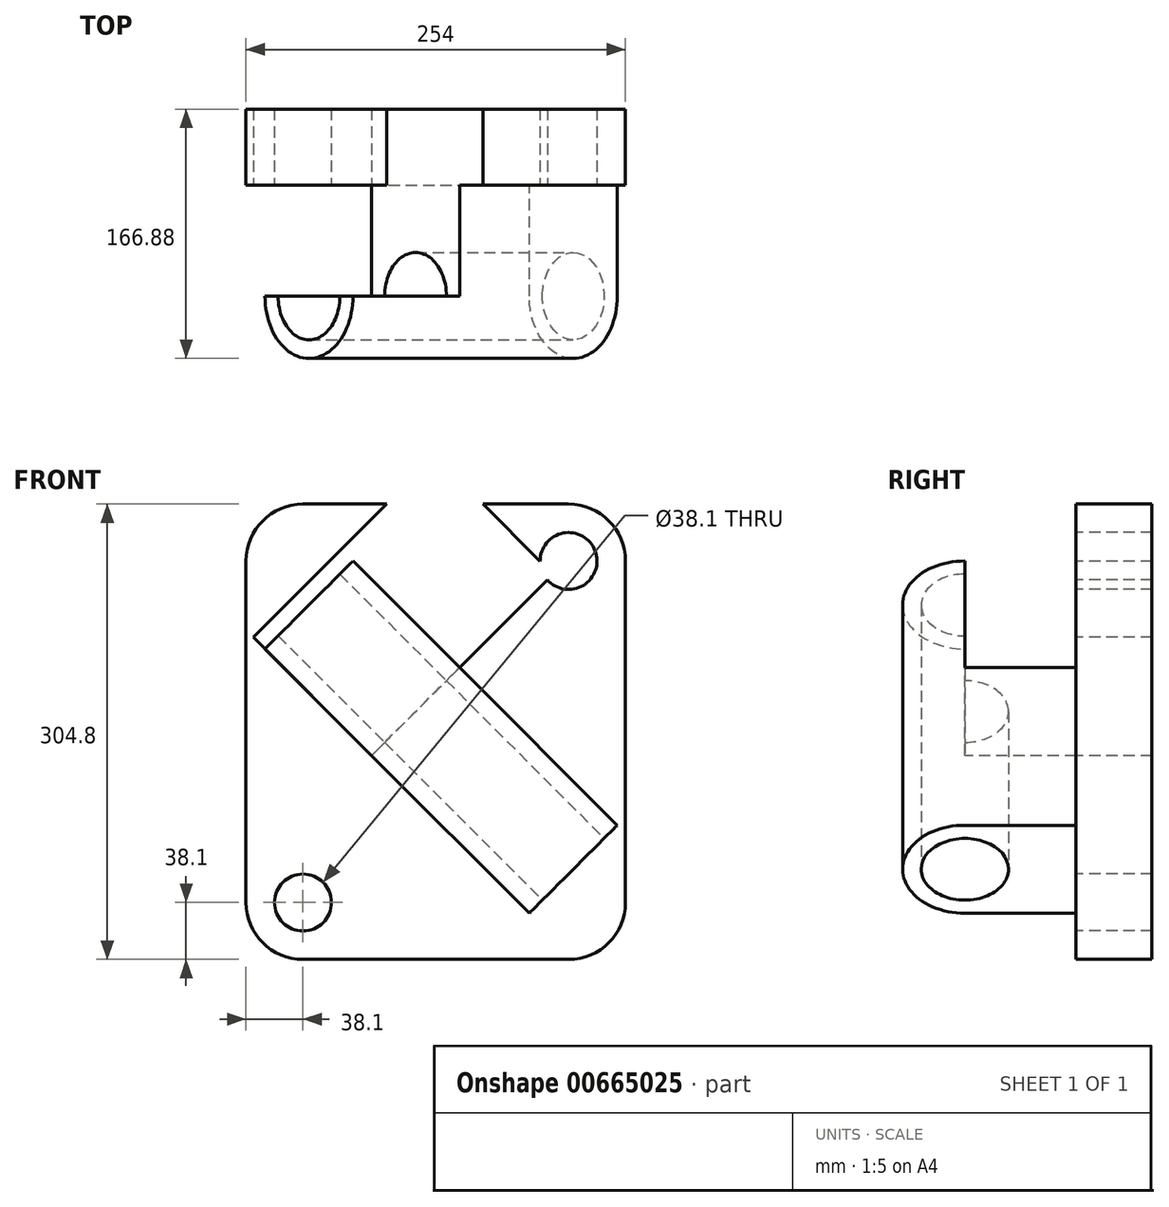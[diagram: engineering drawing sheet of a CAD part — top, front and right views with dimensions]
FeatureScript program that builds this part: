
annotation { "Feature Type Name" : "Feature", "Feature Type Description" : "" }
export const myFeature = defineFeature(function(context is Context, id is Id, definition is map)
    precondition{}
    {
        {
            var Q0;
            Q0=qCreatedBy(makeId("Front.planeOp"),FACE);
            var sketch = newSketch(context, id + "F0", { "sketchPlane" : qUnion([Q0])});
            skLineSegment(sketch, "E0", {"start": v(38.1, 0) * mm, "end": v(215.9, 0) * mm});
            skLineSegment(sketch, "E1", {"start": v(254, 38.1) * mm, "end": v(254, 266.7) * mm});
            skLineSegment(sketch, "E2", {"start": v(215.9, 304.8) * mm, "end": v(38.1, 304.8) * mm});
            skLineSegment(sketch, "E3", {"start": v(0, 266.7) * mm, "end": v(0, 38.1) * mm});
            skPoint(sketch, "E4.visualSharp", {"position": v(0, 304.8) * mm});
            skArc(sketch, "E4.filletArc", {"start": v(38.1, 304.8) * mm, "mid": v(11.16, 293.64) * mm, "end": v(0, 266.7) * mm});
            skPoint(sketch, "E5.visualSharp", {"position": v(254, 304.8) * mm});
            skArc(sketch, "E5.filletArc", {"start": v(254, 266.7) * mm, "mid": v(242.84, 293.64) * mm, "end": v(215.9, 304.8) * mm});
            skPoint(sketch, "E6.visualSharp", {"position": v(254, 0) * mm});
            skArc(sketch, "E6.filletArc", {"start": v(215.9, 0) * mm, "mid": v(242.84, 11.16) * mm, "end": v(254, 38.1) * mm});
            skPoint(sketch, "E7.visualSharp", {"position": v(0, 0) * mm});
            skArc(sketch, "E7.filletArc", {"start": v(0, 38.1) * mm, "mid": v(11.16, 11.16) * mm, "end": v(38.1, 0) * mm});
            skCircle(sketch, "E8", {"center": v(38.1, 38.1) * mm, "radius": 19.05 * mm});
            skCircle(sketch, "E9", {"center": v(215.9, 266.7) * mm, "radius": 19.05 * mm});
            skLineSegment(sketch, "E10", {"start": v(189.58, 30.9) * mm, "end": v(12.67, 207.81) * mm});
            skLineSegment(sketch, "E11.0", {"start": v(248.5, 89.81) * mm, "end": v(71.58, 266.73) * mm});
            skLineSegment(sketch, "E12", {"start": v(248.5, 89.81) * mm, "end": v(189.58, 30.9) * mm});
            skLineSegment(sketch, "E13", {"start": v(12.67, 207.81) * mm, "end": v(71.58, 266.73) * mm});
            skLineSegment(sketch, "E14", {"start": v(0, 38.1) * mm, "end": v(189.58, 30.9) * mm});
            skSolve(sketch);
        }
        {
            var Q0;
            Q0=makeQuery(id+"F0.imprint","IMPRINT",FACE,{"disambiguationData":[TD([[makeQuery(id+"F0.imprint","IMPRINT",EDGE,{"derivedFrom":sQuery(id+"F0.wireOp",EDGE,"E0")}),1.0]])]});
            var Q1;
            Q1=makeQuery(id+"F0.imprint","IMPRINT",FACE,{"disambiguationData":[TD([[makeQuery(id+"F0.imprint","IMPRINT",EDGE,{"derivedFrom":sQuery(id+"F0.wireOp",EDGE,"E10")}),-1.0]])]});
            extrude(context, id + "F1", {"entities" : qUnion([Q0, Q1]), "endBound" : BoundingType.SYMMETRIC, "oppositeDirection" : true, "depth" : 50.8 * mm, "offsetDistance" : 25.4 * mm});
        }
        {
            var Q0;
            Q0=makeQuery(id+"F0.imprint","IMPRINT",FACE,{"disambiguationData":[TD([[makeQuery(id+"F0.imprint","IMPRINT",EDGE,{"derivedFrom":sQuery(id+"F0.wireOp",EDGE,"E10")}),-1.0]])]});
            extrude(context, id + "F2", {"entities" : qUnion([Q0]), "operationType" : NewBodyOperationType.ADD, "depth" : 99.82 * mm, "offsetDistance" : 25.4 * mm});
        }
        {
            var Q0;
            Q0=makeQuery(id+"F2.opExtrude","SWEPT_FACE",FACE,{"disambiguationData":[OSD([sQuery(id+"F0.wireOp",EDGE,"E12")])]});
            var sketch = newSketch(context, id + "F3", { "sketchPlane" : qUnion([Q0])});
            skCircle(sketch, "E15", {"center": v(-99.82, 197.56) * mm, "radius": 29.21 * mm});
            skCircle(sketch, "E16", {"center": v(-99.82, 197.56) * mm, "radius": 41.66 * mm});
            skSolve(sketch);
        }
        {
            var Q0;
            {var subQ0=sQuery(id+"F3.wireOp",EDGE,"E15");var subQ1=sQuery(id+"F0.wireOp",EDGE,"E12");var subQ2=makeQuery(id+"F2.opExtrude","CAP_EDGE",EDGE,{"disambiguationData":[OSD([subQ1])],"isStart":false});var subQ3=makeQuery(id+"F3.imprint","INTERSECT",VERTEX,{"disambiguationData":[OD(0.0)],"derivedFrom":[subQ2,subQ0]});Q0=makeQuery(id+"F3.imprint","IMPRINT",FACE,{"disambiguationData":[TD([[makeQuery(id+"F3.imprint","IMPRINT",EDGE,{"disambiguationData":[TD([[subQ3,1.0]])],"derivedFrom":subQ0}),-1.0]])]});}
            extrude(context, id + "F4", {"entities" : qUnion([Q0]), "operationType" : NewBodyOperationType.ADD, "oppositeDirection" : true, "depth" : 250.2 * mm, "offsetDistance" : 25.4 * mm});
        }
        {
            var Q0;
            {var subQ0=sQuery(id+"F3.wireOp",EDGE,"48uWv1ek-4zHe-EfZB-hBq6-6IiOLvBYJ8zC");var subQ1=makeQuery(id+"F2.opExtrude","CAP_EDGE",EDGE,{"disambiguationData":[OSD([sQuery(id+"F0.wireOp",EDGE,"E12")])],"isStart":false});var subQ2=makeQuery(id+"F3.imprint","INTERSECT",VERTEX,{"disambiguationData":[OD(0.0)],"derivedFrom":[subQ1,subQ0]});Q0=makeQuery(id+"F3.imprint","IMPRINT",FACE,{"disambiguationData":[TD([[makeQuery(id+"F3.imprint","IMPRINT",EDGE,{"disambiguationData":[TD([[subQ2,-1.0]])],"derivedFrom":subQ0}),1.0]])]});}
            var Q1;
            {var subQ0=sQuery(id+"F3.wireOp",EDGE,"E15");var subQ1=makeQuery(id+"F2.opExtrude","CAP_EDGE",EDGE,{"disambiguationData":[OSD([sQuery(id+"F0.wireOp",EDGE,"E12")])],"isStart":false});var subQ2=makeQuery(id+"F3.imprint","INTERSECT",VERTEX,{"disambiguationData":[OD(0.0)],"derivedFrom":[subQ1,subQ0]});Q1=makeQuery(id+"F3.imprint","IMPRINT",FACE,{"disambiguationData":[TD([[makeQuery(id+"F3.imprint","IMPRINT",EDGE,{"disambiguationData":[TD([[subQ2,-1.0]])],"derivedFrom":subQ0}),1.0]])]});}
            extrude(context, id + "F5", {"entities" : qUnion([Q0, Q1]), "operationType" : NewBodyOperationType.REMOVE, "oppositeDirection" : true, "depth" : 250.2 * mm, "offsetDistance" : 25.4 * mm});
        }
        {
            var Q0;
            Q0=makeQuery(id+"F2.opExtrude","SWEPT_FACE",FACE,{"disambiguationData":[OSD([sQuery(id+"F0.wireOp",EDGE,"E10")])]});
            var sketch = newSketch(context, id + "F6", { "sketchPlane" : qUnion([Q0])});
            skLineSegment(sketch, "E17.0", {"start": v(-137.99, 37.08) * mm, "end": v(112.2, 37.08) * mm});
            skLineSegment(sketch, "E18", {"start": v(-137.99, 37.08) * mm, "end": v(-93.54, 37.08) * mm});
            skLineSegment(sketch, "E19", {"start": v(-93.54, 37.08) * mm, "end": v(-93.54, 149.02) * mm});
            skLineSegment(sketch, "E20", {"start": v(-93.54, 149.02) * mm, "end": v(67.75, 149.02) * mm});
            skLineSegment(sketch, "E21", {"start": v(67.75, 149.02) * mm, "end": v(67.75, 37.08) * mm});
            skLineSegment(sketch, "E22", {"start": v(67.75, 37.08) * mm, "end": v(112.2, 37.08) * mm});
            skSolve(sketch);
        }
        {
            var Q0;
            {var subQ0=sQuery(id+"F6.wireOp",EDGE,"E17.0");Q0=makeQuery(id+"F6.imprint","IMPRINT",FACE,{"disambiguationData":[TD([[makeQuery(id+"F6.imprint","IMPRINT",EDGE,{"derivedFrom":subQ0}),1.0]])]});}
            var Q1;
            {var subQ0=sQuery(id+"F6.wireOp",EDGE,"E20");Q1=makeQuery(id+"F6.imprint","IMPRINT",FACE,{"disambiguationData":[TD([[makeQuery(id+"F6.imprint","IMPRINT",EDGE,{"derivedFrom":subQ0}),-1.0]])]});}
            extrude(context, id + "F7", {"entities" : qUnion([Q0, Q1]), "operationType" : NewBodyOperationType.REMOVE, "oppositeDirection" : true, "depth" : 171.7 * mm, "offsetDistance" : 25.4 * mm});
        }
    });
